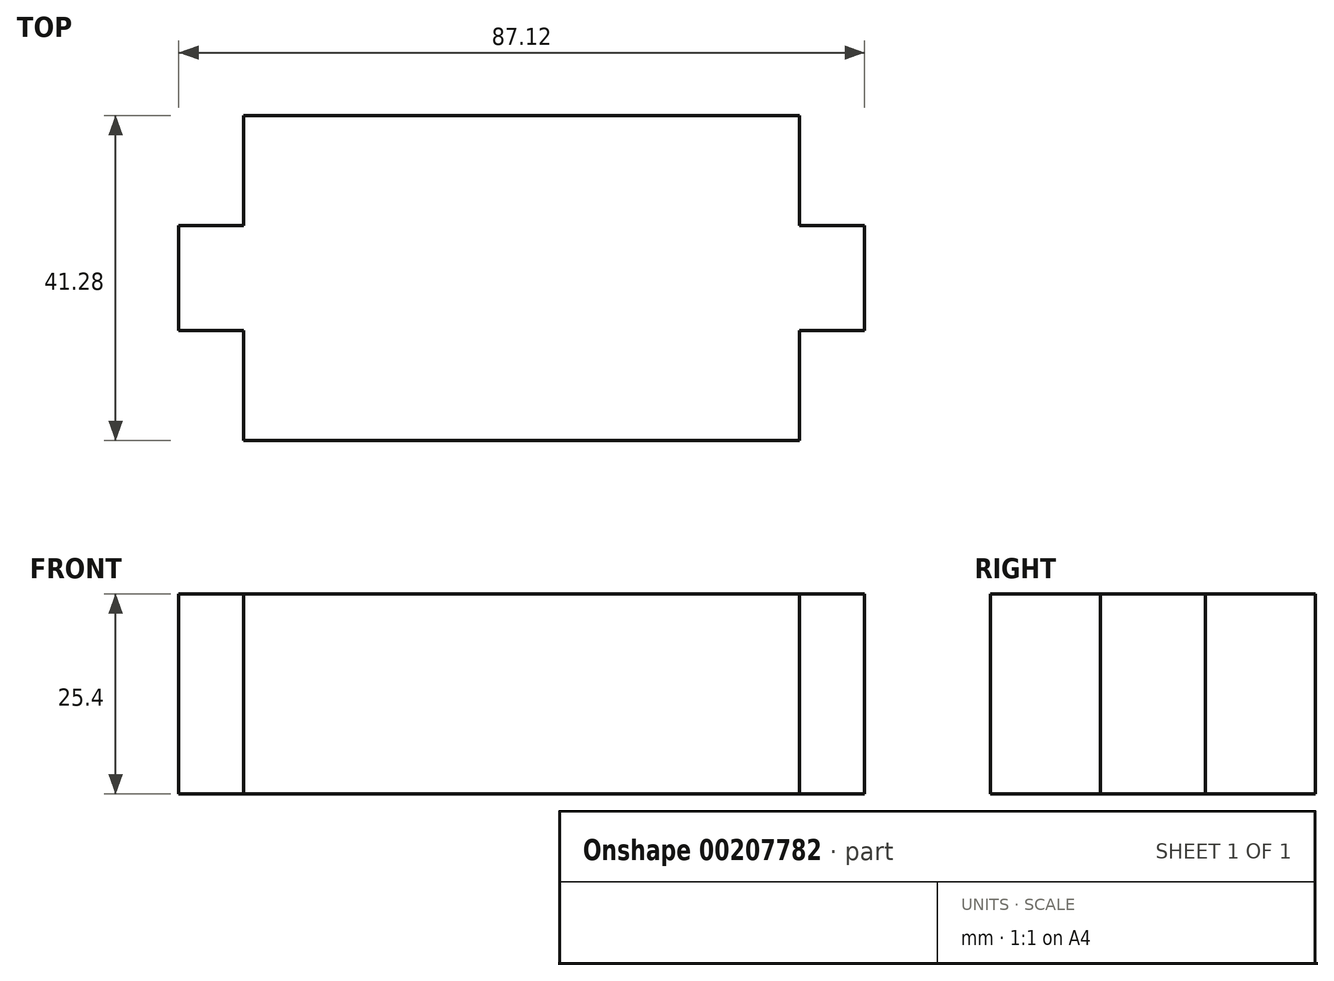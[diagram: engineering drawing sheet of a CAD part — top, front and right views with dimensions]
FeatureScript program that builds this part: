
annotation { "Feature Type Name" : "Feature", "Feature Type Description" : "" }
export const myFeature = defineFeature(function(context is Context, id is Id, definition is map)
    precondition{}
    {
        {
            var Q0;
            Q0=qCreatedBy(makeId("Top.planeOp"),FACE);
            var sketch = newSketch(context, id + "F0", { "sketchPlane" : qUnion([Q0])});
            skLineSegment(sketch, "E0.bottom", {"start": v(35.3, 20.64) * mm, "end": v(-35.3, 20.64) * mm});
            skLineSegment(sketch, "E0.top", {"start": v(35.3, -20.64) * mm, "end": v(-35.3, -20.64) * mm});
            skLineSegment(sketch, "E0.left", {"start": v(35.3, 20.64) * mm, "end": v(35.3, -20.64) * mm});
            skLineSegment(sketch, "E0.right", {"start": v(-35.3, 20.64) * mm, "end": v(-35.3, -20.64) * mm});
            skPoint(sketch, "E0.middle", {"position": v(0, 0) * mm});
            skLineSegment(sketch, "E1.bottom", {"start": v(43.56, 6.67) * mm, "end": v(27.05, 6.67) * mm});
            skLineSegment(sketch, "E1.top", {"start": v(43.56, -6.67) * mm, "end": v(27.05, -6.67) * mm});
            skLineSegment(sketch, "E1.left", {"start": v(43.56, 6.67) * mm, "end": v(43.56, -6.67) * mm});
            skPoint(sketch, "E1.middle", {"position": v(35.3, 0) * mm});
            skLineSegment(sketch, "E2.MirrorCS", {"start": v(-43.56, -6.67) * mm, "end": v(-27.05, -6.67) * mm});
            skLineSegment(sketch, "E3.MirrorCS", {"start": v(-43.56, 6.67) * mm, "end": v(-43.56, -6.67) * mm});
            skLineSegment(sketch, "E4.MirrorCS", {"start": v(-43.56, 6.67) * mm, "end": v(-27.05, 6.67) * mm});
            skSolve(sketch);
        }
        {
            var Q0;
            {var subQ3=sQuery(id+"F0.wireOp",EDGE,"E0.bottom");Q0=makeQuery(id+"F0.imprint","IMPRINT",FACE,{"disambiguationData":[TD([[makeQuery(id+"F0.imprint","IMPRINT",EDGE,{"derivedFrom":subQ3}),1.0]])]});}
            var Q1;
            {var subQ5=sQuery(id+"F0.wireOp",EDGE,"E3.MirrorCS");Q1=makeQuery(id+"F0.imprint","IMPRINT",FACE,{"disambiguationData":[TD([[makeQuery(id+"F0.imprint","IMPRINT",EDGE,{"derivedFrom":subQ5}),1.0]])]});}
            var Q2;
            {var subQ5=sQuery(id+"F0.wireOp",EDGE,"E1.left");Q2=makeQuery(id+"F0.imprint","IMPRINT",FACE,{"disambiguationData":[TD([[makeQuery(id+"F0.imprint","IMPRINT",EDGE,{"derivedFrom":subQ5}),-1.0]])]});}
            extrude(context, id + "F1", {"entities" : qUnion([Q0, Q1, Q2]), "endBound" : BoundingType.SYMMETRIC, "depth" : 25.4 * mm});
        }
    });
